# Revit family: HL_RU_Roof drain_HL64BP-B-221103
name_source: partatom
category: Sanitärinstallationen
units: mm (PartAtom-declared; Revit-internal decimal feet)

## family parameters
Arbeitsebenenbasiert = Nein
Beim Laden mit Abzugskörper schneiden = Nein
Bemaßung runder Anschluss = Durchmesser verwenden
Gemeinsam genutzt = Nein
Immer vertikal = Ja
OmniClass-Nummer = 23.70.50.21.24.14
OmniClass-Titel = Deck Waste Water Drains
Raumberechnungspunkt = Ja
Teiletyp = Normal

## types (2) — shared parameters
Abwasserrohrverbindung = Ja
Beschreibung = Кровельные воронки
HW-Verbindung = Nein
Hersteller = HL Hutterer & Lechner GmbH
KW-Verbindung = Nein
Lüftungsverbindung = Nein
URL = http://www.hutterer-lechner.com
МАКСИМАЛЬНАЯ НАГРУЗКА КЛАССА = K - 300 kg
МАТЕРИАЛ = PVC
НАСАДКА = 19-65mm/148x148mm
ПРОИЗВОДИТЕЛЬНОСТЬ = 3,7 l/s
РЕШЁТКА = Edelstahl 137x137mm
zero-valued in all types: Vorgabe-Ansicht

## per-type parameters (varying)
| type | Bauelement | EAN | Modell | Typenkommentare | ВЕС | НОМИНАЛЬНЫЙ ДИАМЕТР | РАЗМЕР |
| HL_Кровельная воронка_HL64BP_1 | HL64BP_1 | 9003076031504 | HL64BP_1 | HL64BP/1 Кровельная воронка DN110 для эксплуатируемой кровли, горизонтальный выпуск, с ПВХ_фланцем, | 1,34 [kg] | 110 mm | DN110 |
| HL_Кровельная воронка_HL64BP_7 | HL64BP_7 | 9003076031481 | HL64BP_7 | HL64BP/7 Кровельная воронка DN75 для эксплуатируемой кровли, горизонтальный выпуск, с ПВХ_фланцем, | 1,75 [kg] | 75 mm | DN75 |

## geometry (parser evidence)
native form markers: Sweep x5
no freeform markers — native parametric forms only
